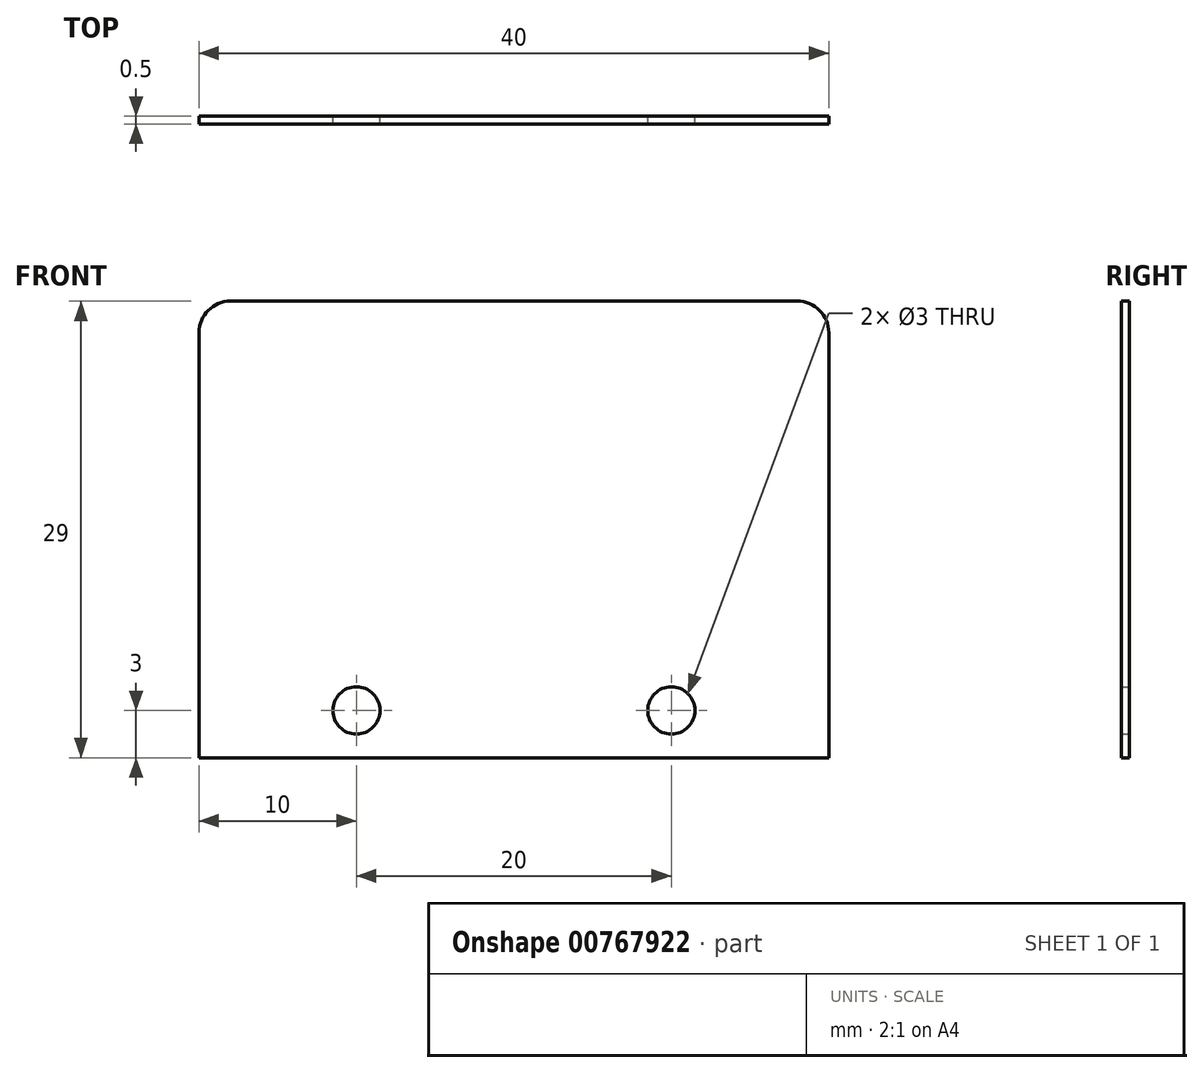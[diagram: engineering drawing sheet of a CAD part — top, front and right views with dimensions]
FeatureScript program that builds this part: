
annotation { "Feature Type Name" : "Feature", "Feature Type Description" : "" }
export const myFeature = defineFeature(function(context is Context, id is Id, definition is map)
    precondition{}
    {
        {
            var Q0;
            Q0=qCreatedBy(makeId("Front.planeOp"),FACE);
            var sketch = newSketch(context, id + "F0", { "sketchPlane" : qUnion([Q0])});
            skLineSegment(sketch, "E0.top", {"start": v(2, 40) * mm, "end": v(38, 40) * mm});
            skLineSegment(sketch, "E0.right", {"start": v(40, 11) * mm, "end": v(40, 38) * mm});
            skLineSegment(sketch, "E1", {"start": v(0, 20) * mm, "end": v(40, 20) * mm, "construction": true});
            skLineSegment(sketch, "E2.0", {"start": v(0, 17) * mm, "end": v(40, 17) * mm, "construction": true});
            skLineSegment(sketch, "E3", {"start": v(5, 43.59) * mm, "end": v(5, 11) * mm, "construction": true});
            skLineSegment(sketch, "E4", {"start": v(35, 43.3) * mm, "end": v(35, 11) * mm, "construction": true});
            skLineSegment(sketch, "E5.0", {"start": v(0, 11) * mm, "end": v(40, 11) * mm});
            skPoint(sketch, "E6.visualSharp", {"position": v(0, 40) * mm});
            skArc(sketch, "E6.filletArc", {"start": v(2, 40) * mm, "mid": v(0.59, 39.41) * mm, "end": v(0, 38) * mm});
            skPoint(sketch, "E7.visualSharp", {"position": v(40, 40) * mm});
            skArc(sketch, "E7.filletArc", {"start": v(40, 38) * mm, "mid": v(39.41, 39.41) * mm, "end": v(38, 40) * mm});
            skCircle(sketch, "E8", {"center": v(10, 14) * mm, "radius": 1.5 * mm});
            skLineSegment(sketch, "E9", {"start": v(20, 17) * mm, "end": v(20, 11) * mm, "construction": true});
            skCircle(sketch, "E10.MirrorC", {"center": v(30, 14) * mm, "radius": 1.5 * mm});
            skLineSegment(sketch, "E11.trimOffspring", {"start": v(0, 11) * mm, "end": v(0, 38) * mm});
            skPoint(sketch, "E0.bottom.start.orphan", {"position": v(0, 0) * mm});
            skSolve(sketch);
        }
        {
            var Q0;
            Q0=makeQuery(id+"F0.imprint","IMPRINT",FACE,{"disambiguationData":[TD([[makeQuery(id+"F0.imprint","IMPRINT",EDGE,{"derivedFrom":sQuery(id+"F0.wireOp",EDGE,"E0.top")}),-1.0]])]});
            extrude(context, id + "F1", {"entities" : qUnion([Q0]), "depth" : 0.5 * mm, "offsetDistance" : 25 * mm});
        }
    });
